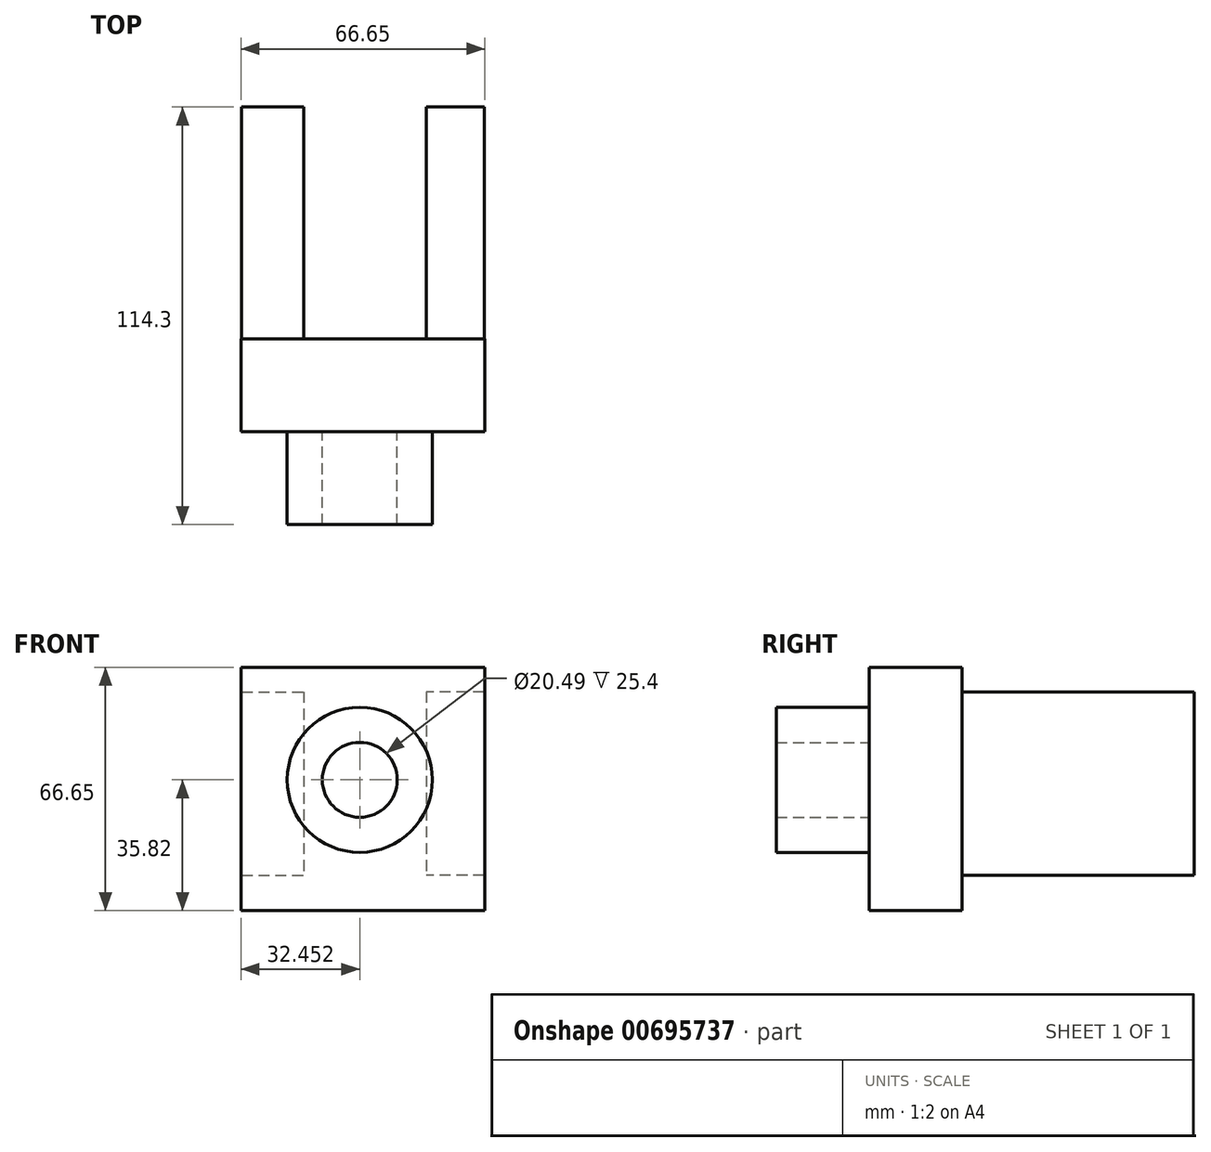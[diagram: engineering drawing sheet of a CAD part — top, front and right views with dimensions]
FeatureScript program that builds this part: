
annotation { "Feature Type Name" : "Feature", "Feature Type Description" : "" }
export const myFeature = defineFeature(function(context is Context, id is Id, definition is map)
    precondition{}
    {
        {
            var Q0;
            Q0=qCreatedBy(makeId("Front.planeOp"),FACE);
            var sketch = newSketch(context, id + "F0", { "sketchPlane" : qUnion([Q0])});
            skLineSegment(sketch, "E0.bottom", {"start": v(-94.25, 30.83) * mm, "end": v(-60.93, 30.83) * mm});
            skLineSegment(sketch, "E0.top", {"start": v(-94.25, -35.82) * mm, "end": v(-60.93, -35.82) * mm});
            skLineSegment(sketch, "E0.left", {"start": v(-94.25, 30.83) * mm, "end": v(-94.25, -35.82) * mm});
            skLineSegment(sketch, "E0.right", {"start": v(-60.93, 30.83) * mm, "end": v(-60.93, -35.82) * mm});
            skLineSegment(sketch, "E1.MirrorCS", {"start": v(-94.25, 30.83) * mm, "end": v(-127.58, 30.83) * mm});
            skLineSegment(sketch, "E2.MirrorCS", {"start": v(-127.58, 30.83) * mm, "end": v(-127.58, -35.82) * mm});
            skLineSegment(sketch, "E3.MirrorCS", {"start": v(-94.25, -35.82) * mm, "end": v(-127.58, -35.82) * mm});
            skSolve(sketch);
        }
        {
            var Q0;
            Q0 = qSketchRegion(id + "F0", true);
            extrude(context, id + "F1", {"entities" : qUnion([Q0]), "depth" : 25.4 * mm, "offsetDistance" : 25.4 * mm});
        }
        {
            var Q0;
            Q0=qCreatedBy(makeId("Front.planeOp"),FACE);
            var sketch = newSketch(context, id + "F2", { "sketchPlane" : qUnion([Q0])});
            skLineSegment(sketch, "E4.bottom", {"start": v(-127.43, 24.08) * mm, "end": v(-110.4, 24.08) * mm});
            skLineSegment(sketch, "E4.top", {"start": v(-127.43, -26.13) * mm, "end": v(-110.4, -26.13) * mm});
            skLineSegment(sketch, "E4.left", {"start": v(-127.43, 24.08) * mm, "end": v(-127.43, -26.13) * mm});
            skLineSegment(sketch, "E4.right", {"start": v(-110.4, 24.08) * mm, "end": v(-110.4, -26.13) * mm});
            skPoint(sketch, "E5.right.start.orphan", {"position": v(19.97, 24.08) * mm});
            skPoint(sketch, "E5.top.end.orphan", {"position": v(19.97, -26.13) * mm});
            skLineSegment(sketch, "E6.bottom", {"start": v(-61.07, 24.08) * mm, "end": v(-76.92, 24.08) * mm});
            skLineSegment(sketch, "E6.top", {"start": v(-61.07, -26.13) * mm, "end": v(-76.92, -26.13) * mm});
            skLineSegment(sketch, "E6.left", {"start": v(-61.07, 24.08) * mm, "end": v(-61.07, -26.13) * mm});
            skLineSegment(sketch, "E6.right", {"start": v(-76.92, 24.08) * mm, "end": v(-76.92, -26.13) * mm});
            skSolve(sketch);
        }
        {
            var Q0;
            Q0 = qSketchRegion(id + "F2", true);
            extrude(context, id + "F3", {"entities" : qUnion([Q0]), "operationType" : NewBodyOperationType.ADD, "oppositeDirection" : true, "depth" : 63.5 * mm, "offsetDistance" : 25.4 * mm});
        }
        {
            var Q0;
            Q0=qCreatedBy(makeId("Front.planeOp"),FACE);
            var sketch = newSketch(context, id + "F4", { "sketchPlane" : qUnion([Q0])});
            skCircle(sketch, "E7", {"center": v(-95.13, 0) * mm, "radius": 19.86 * mm});
            skCircle(sketch, "E8", {"center": v(-95.13, 0) * mm, "radius": 10.24 * mm});
            skSolve(sketch);
        }
        {
            var Q0;
            Q0 = qSketchRegion(id + "F4", true);
            extrude(context, id + "F5", {"entities" : qUnion([Q0]), "operationType" : NewBodyOperationType.ADD, "depth" : 50.8 * mm, "offsetDistance" : 25.4 * mm});
        }
    });
